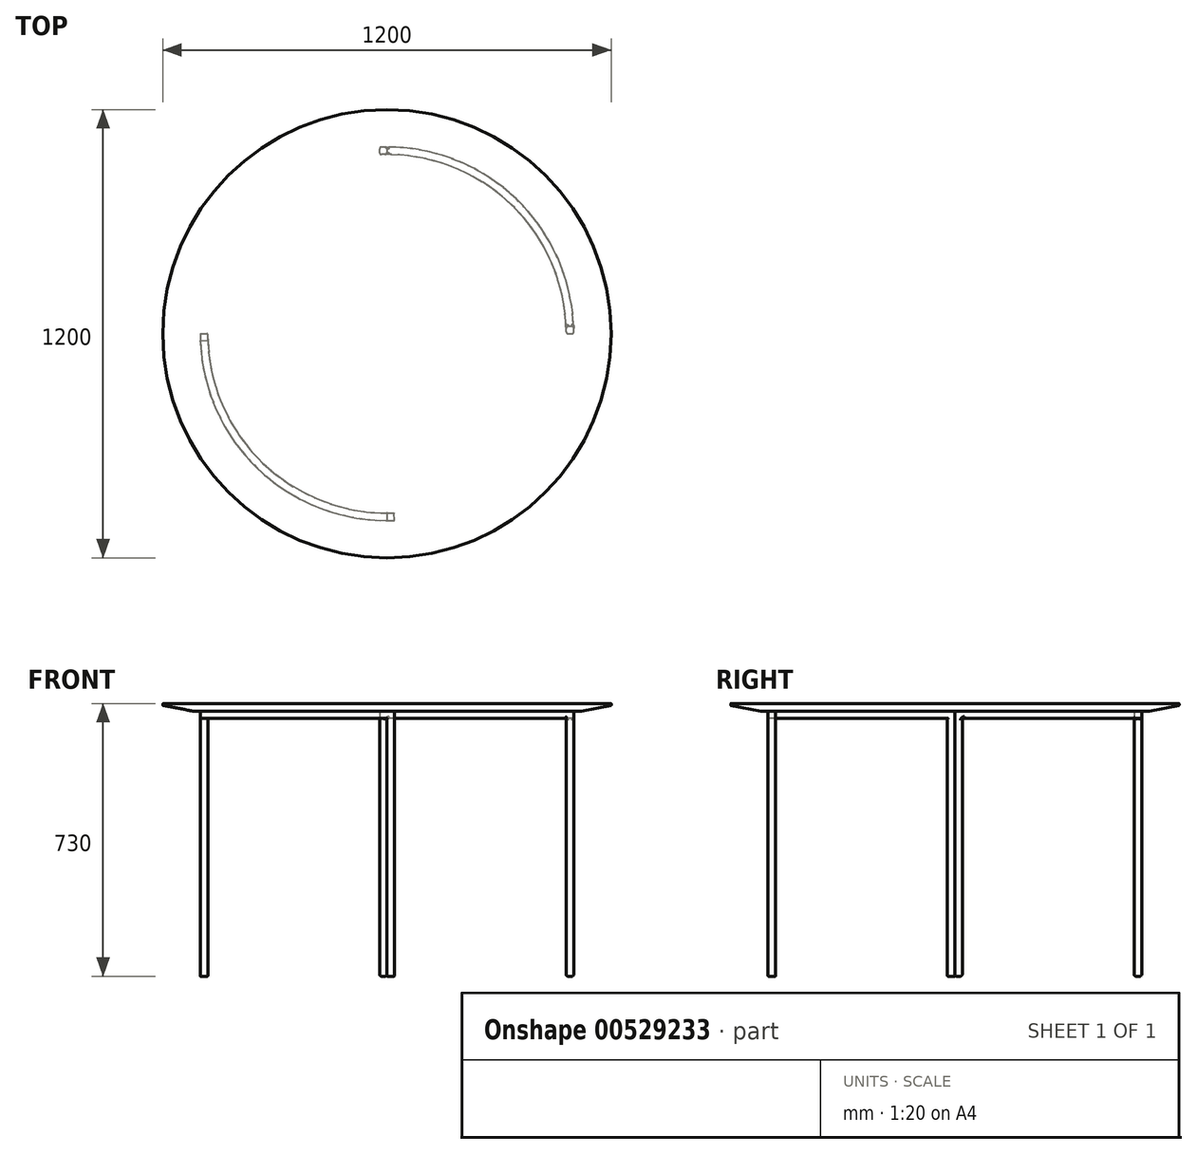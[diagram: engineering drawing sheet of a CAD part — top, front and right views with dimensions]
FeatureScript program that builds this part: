
annotation { "Feature Type Name" : "Feature", "Feature Type Description" : "" }
export const myFeature = defineFeature(function(context is Context, id is Id, definition is map)
    precondition{}
    {
        {
            var Q0;
            Q0=qCreatedBy(makeId("Top.planeOp"),FACE);
            var sketch = newSketch(context, id + "F0", { "sketchPlane" : qUnion([Q0])});
            skArc(sketch, "E0", {"start": v(0, -500) * mm, "mid": v(10, -499.9) * mm, "end": v(20, -499.6) * mm});
            skArc(sketch, "E1.0", {"start": v(0, -480) * mm, "mid": v(9.6, -479.9) * mm, "end": v(19.2, -479.62) * mm});
            skLineSegment(sketch, "E2", {"start": v(0, 500) * mm, "end": v(0, 480) * mm});
            skLineSegment(sketch, "E3", {"start": v(-500, 0) * mm, "end": v(-480, 0) * mm});
            skLineSegment(sketch, "E4", {"start": v(20, -499.6) * mm, "end": v(19.2, -479.62) * mm});
            skLineSegment(sketch, "E5", {"start": v(499.6, 20) * mm, "end": v(479.62, 19.2) * mm});
            skLineSegment(sketch, "E6.trimOffspring", {"start": v(0, -480) * mm, "end": v(0, -500) * mm});
            skLineSegment(sketch, "E7.trimOffspring", {"start": v(-19.2, 479.62) * mm, "end": v(-20, 499.6) * mm});
            skLineSegment(sketch, "E8.trimOffspring", {"start": v(480, 0) * mm, "end": v(500, 0) * mm});
            skLineSegment(sketch, "E9.trimOffspring", {"start": v(-479.62, -19.2) * mm, "end": v(-499.6, -20) * mm});
            skArc(sketch, "E10.trimOffspring", {"start": v(0, 480) * mm, "mid": v(-9.6, 479.9) * mm, "end": v(-19.2, 479.62) * mm});
            skArc(sketch, "E11.trimOffspring", {"start": v(0, 500) * mm, "mid": v(-10, 499.9) * mm, "end": v(-20, 499.6) * mm});
            skArc(sketch, "E12.trimOffspring", {"start": v(-500, 0) * mm, "mid": v(-499.9, -10) * mm, "end": v(-499.6, -20) * mm});
            skArc(sketch, "E13.trimOffspring", {"start": v(-480, 0) * mm, "mid": v(-479.9, -9.6) * mm, "end": v(-479.62, -19.2) * mm});
            skArc(sketch, "E14.trimOffspring", {"start": v(480, 0) * mm, "mid": v(479.9, 9.6) * mm, "end": v(479.62, 19.2) * mm});
            skArc(sketch, "E15.trimOffspring", {"start": v(500, 0) * mm, "mid": v(499.9, 10) * mm, "end": v(499.6, 20) * mm});
            skSolve(sketch);
        }
        {
            var Q0;
            Q0 = qSketchRegion(id + "F0", true);
            extrude(context, id + "F1", {"entities" : qUnion([Q0]), "depth" : 690 * mm, "offsetDistance" : 25 * mm});
        }
        {
            var Q0;
            Q0=makeQuery(id+"F1.opExtrude","CAP_FACE",FACE,{"disambiguationData":[OSD([sQuery(id+"F0.wireOp",EDGE,"E2"),sQuery(id+"F0.wireOp",EDGE,"E7.trimOffspring"),sQuery(id+"F0.wireOp",EDGE,"E10.trimOffspring"),sQuery(id+"F0.wireOp",EDGE,"E11.trimOffspring")])],"isStart":false});
            var sketch = newSketch(context, id + "F2", { "sketchPlane" : qUnion([Q0])});
            skArc(sketch, "E16", {"start": v(-500, 0) * mm, "mid": v(-346.41, -360.55) * mm, "end": v(20, -499.6) * mm});
            skArc(sketch, "E17.0", {"start": v(-480, 0) * mm, "mid": v(-332.56, -346.13) * mm, "end": v(19.2, -479.62) * mm});
            skLineSegment(sketch, "E18", {"start": v(-500, 0) * mm, "end": v(-480, 0) * mm});
            skLineSegment(sketch, "E19.trimOffspring", {"start": v(480, 0) * mm, "end": v(500, 0) * mm});
            skLineSegment(sketch, "E20", {"start": v(20, -499.6) * mm, "end": v(19.2, -479.62) * mm});
            skLineSegment(sketch, "E21.trimOffspring", {"start": v(-19.2, 479.62) * mm, "end": v(-20, 499.6) * mm});
            skArc(sketch, "E22.trimOffspring", {"start": v(480, 0) * mm, "mid": v(332.56, 346.13) * mm, "end": v(-19.2, 479.62) * mm});
            skArc(sketch, "E23.trimOffspring", {"start": v(500, 0) * mm, "mid": v(346.41, 360.55) * mm, "end": v(-20, 499.6) * mm});
            skPoint(sketch, "E24.start.orphan", {"position": v(-499.6, -20) * mm});
            skPoint(sketch, "E25.start.orphan", {"position": v(0, -500) * mm});
            skPoint(sketch, "E26.trimOffspring.end.orphan", {"position": v(0, 500) * mm});
            skSolve(sketch);
        }
        {
            var Q0;
            Q0 = qSketchRegion(id + "F2", true);
            extrude(context, id + "F3", {"entities" : qUnion([Q0]), "operationType" : NewBodyOperationType.ADD, "depth" : 20 * mm, "offsetDistance" : 25 * mm});
        }
        {
            var Q0;
            Q0=makeQuery(id+"F3.opExtrude","CAP_FACE",FACE,{"disambiguationData":[OSD([sQuery(id+"F2.wireOp",EDGE,"E19.trimOffspring"),sQuery(id+"F2.wireOp",EDGE,"E21.trimOffspring"),sQuery(id+"F2.wireOp",EDGE,"E22.trimOffspring"),sQuery(id+"F2.wireOp",EDGE,"E23.trimOffspring")])],"isStart":false});
            var sketch = newSketch(context, id + "F4", { "sketchPlane" : qUnion([Q0])});
            skCircle(sketch, "E27", {"center": v(0, 0) * mm, "radius": 600 * mm});
            skSolve(sketch);
        }
        {
            var Q0;
            Q0 = qSketchRegion(id + "F4", true);
            extrude(context, id + "F5", {"entities" : qUnion([Q0]), "depth" : 20 * mm, "offsetDistance" : 25 * mm});
        }
        {
            var Q0;
            Q0=qCreatedBy(makeId("Front.planeOp"),FACE);
            var sketch = newSketch(context, id + "F6", { "sketchPlane" : qUnion([Q0])});
            skLineSegment(sketch, "E28", {"start": v(520, 710) * mm, "end": v(600, 725) * mm});
            skLineSegment(sketch, "E29", {"start": v(600, 725) * mm, "end": v(600, 694.84) * mm});
            skLineSegment(sketch, "E30", {"start": v(600, 694.84) * mm, "end": v(520, 710) * mm});
            skLineSegment(sketch, "E31", {"start": v(0, 0) * mm, "end": v(0, 667.55) * mm, "construction": true});
            skSolve(sketch);
        }
        {
            var Q0;
            Q0 = qSketchRegion(id + "F6", true);
            var Q1;
            Q1=sQuery(id+"F6.wireOp",EDGE,"E31");
            revolve(context, id + "F7", {"operationType" : NewBodyOperationType.REMOVE, "entities" : qUnion([Q0]), "axis" : qUnion([Q1]), "revolveType" : RevolveType.FULL, "oppositeDirection" : true});
        }
        {
            var Q0;
            Q0=makeQuery(id+"F5.opExtrude","SWEPT_FACE",FACE,{"disambiguationData":[OSD([sQuery(id+"F4.wireOp",EDGE,"E27")])]});
            var Q1;
            Q1=makeQuery(id+"F7.boolean.opBoolean","COPY",FACE,{"derivedFrom":makeQuery(id+"F7.opRevolve","SWEPT_FACE",FACE,{"disambiguationData":[OSD([sQuery(id+"F6.wireOp",EDGE,"E28")])]})});
            fillet(context, id + "F8", {"entities" : qUnion([Q0, Q1]), "radius" : 1 * mm, "tangentPropagation" : true, "allowEdgeOverflow" : false});
        }
        {
            var Q0;
            Q0=makeQuery(id+"F3.boolean.opBoolean","MERGE",FACE,{"derivedFrom":[makeQuery(id+"F1.opExtrude","SWEPT_FACE",FACE,{"disambiguationData":[OSD([sQuery(id+"F0.wireOp",EDGE,"E0")])]}),makeQuery(id+"F1.opExtrude","SWEPT_FACE",FACE,{"disambiguationData":[OSD([sQuery(id+"F0.wireOp",EDGE,"E12.trimOffspring")])]}),makeQuery(id+"F3.opExtrude","SWEPT_FACE",FACE,{"disambiguationData":[OSD([sQuery(id+"F2.wireOp",EDGE,"E16")])]})]});
            var Q1;
            Q1=makeQuery(id+"F3.boolean.opBoolean","MERGE",FACE,{"derivedFrom":[makeQuery(id+"F1.opExtrude","SWEPT_FACE",FACE,{"disambiguationData":[OSD([sQuery(id+"F0.wireOp",EDGE,"E4")])]}),makeQuery(id+"F3.opExtrude","SWEPT_FACE",FACE,{"disambiguationData":[OSD([sQuery(id+"F2.wireOp",EDGE,"E20")])]})]});
            var Q2;
            Q2=makeQuery(id+"F3.boolean.opBoolean","MERGE",FACE,{"derivedFrom":[makeQuery(id+"F1.opExtrude","SWEPT_FACE",FACE,{"disambiguationData":[OSD([sQuery(id+"F0.wireOp",EDGE,"E1.0")])]}),makeQuery(id+"F1.opExtrude","SWEPT_FACE",FACE,{"disambiguationData":[OSD([sQuery(id+"F0.wireOp",EDGE,"E13.trimOffspring")])]}),makeQuery(id+"F3.opExtrude","SWEPT_FACE",FACE,{"disambiguationData":[OSD([sQuery(id+"F2.wireOp",EDGE,"E17.0")])]})]});
            var Q3;
            Q3=makeQuery(id+"F3.opExtrude","CAP_FACE",FACE,{"disambiguationData":[OSD([sQuery(id+"F2.wireOp",EDGE,"E16"),sQuery(id+"F2.wireOp",EDGE,"E17.0"),sQuery(id+"F2.wireOp",EDGE,"E18"),sQuery(id+"F2.wireOp",EDGE,"E20")])],"isStart":true});
            var Q4;
            Q4=makeQuery(id+"F3.boolean.opBoolean","MERGE",FACE,{"derivedFrom":[makeQuery(id+"F1.opExtrude","SWEPT_FACE",FACE,{"disambiguationData":[OSD([sQuery(id+"F0.wireOp",EDGE,"E3")])]}),makeQuery(id+"F3.opExtrude","SWEPT_FACE",FACE,{"disambiguationData":[OSD([sQuery(id+"F2.wireOp",EDGE,"E18")])]})]});
            var Q5;
            Q5=makeQuery(id+"F1.opExtrude","SWEPT_FACE",FACE,{"disambiguationData":[OSD([sQuery(id+"F0.wireOp",EDGE,"E6.trimOffspring")])]});
            var Q6;
            Q6=makeQuery(id+"F1.opExtrude","SWEPT_FACE",FACE,{"disambiguationData":[OSD([sQuery(id+"F0.wireOp",EDGE,"E9.trimOffspring")])]});
            fillet(context, id + "F9", {"entities" : qUnion([Q0, Q1, Q2, Q3, Q4, Q5, Q6]), "radius" : 1 * mm, "tangentPropagation" : true, "allowEdgeOverflow" : false});
        }
        {
            var Q0;
            Q0=makeQuery(id+"F3.boolean.opBoolean","MERGE",FACE,{"derivedFrom":[makeQuery(id+"F1.opExtrude","SWEPT_FACE",FACE,{"disambiguationData":[OSD([sQuery(id+"F0.wireOp",EDGE,"E11.trimOffspring")])]}),makeQuery(id+"F1.opExtrude","SWEPT_FACE",FACE,{"disambiguationData":[OSD([sQuery(id+"F0.wireOp",EDGE,"E15.trimOffspring")])]}),makeQuery(id+"F3.opExtrude","SWEPT_FACE",FACE,{"disambiguationData":[OSD([sQuery(id+"F2.wireOp",EDGE,"E23.trimOffspring")])]})]});
            var Q1;
            Q1=makeQuery(id+"F3.boolean.opBoolean","MERGE",FACE,{"derivedFrom":[makeQuery(id+"F1.opExtrude","SWEPT_FACE",FACE,{"disambiguationData":[OSD([sQuery(id+"F0.wireOp",EDGE,"E10.trimOffspring")])]}),makeQuery(id+"F1.opExtrude","SWEPT_FACE",FACE,{"disambiguationData":[OSD([sQuery(id+"F0.wireOp",EDGE,"E14.trimOffspring")])]}),makeQuery(id+"F3.opExtrude","SWEPT_FACE",FACE,{"disambiguationData":[OSD([sQuery(id+"F2.wireOp",EDGE,"E22.trimOffspring")])]})]});
            var Q2;
            Q2=makeQuery(id+"F3.opExtrude","CAP_FACE",FACE,{"disambiguationData":[OSD([sQuery(id+"F2.wireOp",EDGE,"E19.trimOffspring"),sQuery(id+"F2.wireOp",EDGE,"E21.trimOffspring"),sQuery(id+"F2.wireOp",EDGE,"E22.trimOffspring"),sQuery(id+"F2.wireOp",EDGE,"E23.trimOffspring")])],"isStart":true});
            var Q3;
            Q3=makeQuery(id+"F3.boolean.opBoolean","MERGE",FACE,{"derivedFrom":[makeQuery(id+"F1.opExtrude","SWEPT_FACE",FACE,{"disambiguationData":[OSD([sQuery(id+"F0.wireOp",EDGE,"E8.trimOffspring")])]}),makeQuery(id+"F3.opExtrude","SWEPT_FACE",FACE,{"disambiguationData":[OSD([sQuery(id+"F2.wireOp",EDGE,"E19.trimOffspring")])]})]});
            var Q4;
            Q4=makeQuery(id+"F1.opExtrude","SWEPT_EDGE",EDGE,{"disambiguationData":[OSD([sQuery(id+"F0.wireOp",EDGE,"E5"),sQuery(id+"F0.wireOp",EDGE,"E15.trimOffspring")])]});
            var Q5;
            Q5=makeQuery(id+"F1.opExtrude","SWEPT_FACE",FACE,{"disambiguationData":[OSD([sQuery(id+"F0.wireOp",EDGE,"E5")])]});
            var Q6;
            Q6=makeQuery(id+"F3.boolean.opBoolean","MERGE",FACE,{"derivedFrom":[makeQuery(id+"F1.opExtrude","SWEPT_FACE",FACE,{"disambiguationData":[OSD([sQuery(id+"F0.wireOp",EDGE,"E7.trimOffspring")])]}),makeQuery(id+"F3.opExtrude","SWEPT_FACE",FACE,{"disambiguationData":[OSD([sQuery(id+"F2.wireOp",EDGE,"E21.trimOffspring")])]})]});
            var Q7;
            Q7=makeQuery(id+"F1.opExtrude","SWEPT_FACE",FACE,{"disambiguationData":[OSD([sQuery(id+"F0.wireOp",EDGE,"E2")])]});
            fillet(context, id + "F10", {"entities" : qUnion([Q0, Q1, Q2, Q3, Q4, Q5, Q6, Q7]), "radius" : 5 * mm, "tangentPropagation" : true, "allowEdgeOverflow" : false});
        }
    });
